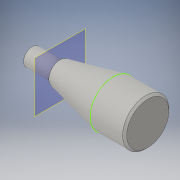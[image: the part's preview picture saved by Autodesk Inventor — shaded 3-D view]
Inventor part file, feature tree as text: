
AUTODESK INVENTOR PART (.ipt)
format: ipt  version: 2016 (Build 200138000, 138)  size: 117,760 bytes
history: native  units: in
note: dims shown in document units (in); Inventor stores cm internally (conversion verified against a paired STEP export)
features: sketch x4, extrude x2, chamfer x1, plane x1, loft x1, other x1
ambient origin geometry x8: Origin, YZ Plane, XZ Plane, XY Plane, X Axis, Y Axis, Z Axis, Center Point
bodies: Solid1 (feature_tree)
feature tree (10):
  extrude  "Extrusion1"  Depth=0.75in TaperAngle=0.0deg
  chamfer  "Chamfer1"  Distance=0.045in Angle=45.0deg
  sketch  "Sketch2"  dims[d6=1.15in d7=0.48in]
  plane  "Work Plane1"
  loft  "Loft1"
  extrude  "Extrusion2"  TaperAngle=0.0deg  [1 undecoded]
  sketch  "Sketch1"  dims[d0=1.0in d1=0.75in d2=0.0in d3=0.045in d4=0.125in d5=45.0deg]
  sketch  "Sketch3"  dims[d8=0.0in d9=90.0deg d10=0.0in d11=90.0deg]
  other  "Edges1"
  sketch  "Sketch4"  dims[d12=0.375in d13=0.6in d14=0.0in]
note: 1 required parameter value undecoded (feature->parameter linkage not recoverable at this tier; creation-order binding heuristic only, values carry confidence <= 0.55)
